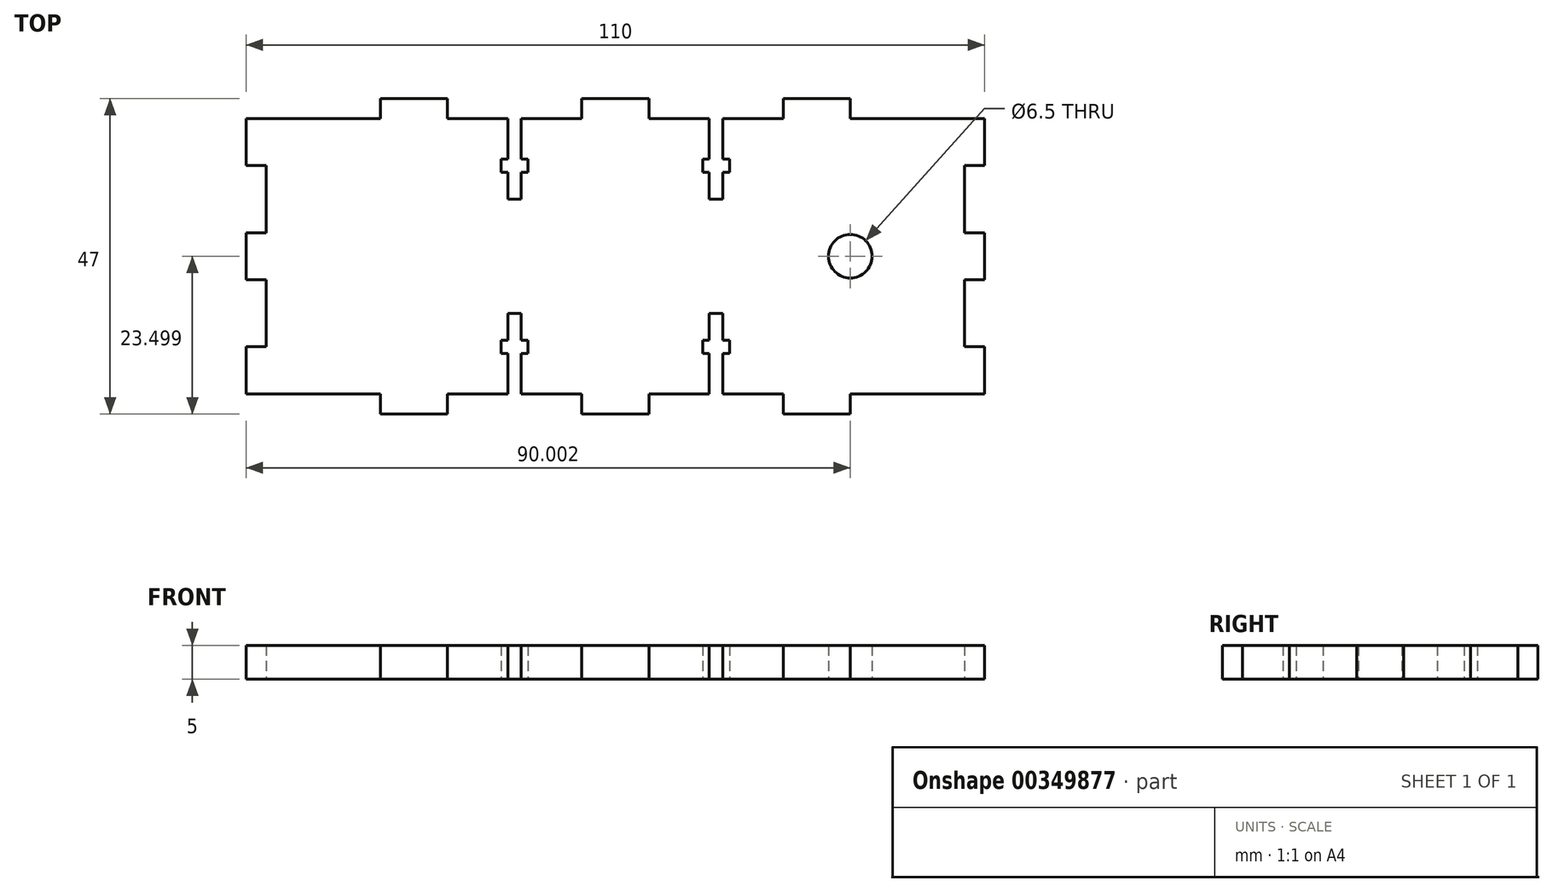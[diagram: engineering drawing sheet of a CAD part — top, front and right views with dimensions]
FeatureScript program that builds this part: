
annotation { "Feature Type Name" : "Feature", "Feature Type Description" : "" }
export const myFeature = defineFeature(function(context is Context, id is Id, definition is map)
    precondition{}
    {
        {
            var Q0;
            Q0=qCreatedBy(makeId("Top.planeOp"),FACE);
            var sketch = newSketch(context, id + "F0", { "sketchPlane" : qUnion([Q0])});
            skLineSegment(sketch, "E0", {"start": v(-63.5, 47.22) * mm, "end": v(-63.5, 40.22) * mm});
            skLineSegment(sketch, "E1", {"start": v(-63.5, 40.22) * mm, "end": v(-60.5, 40.22) * mm});
            skLineSegment(sketch, "E2", {"start": v(-60.5, 40.22) * mm, "end": v(-60.5, 30.22) * mm});
            skLineSegment(sketch, "E3", {"start": v(-60.5, 30.22) * mm, "end": v(-63.5, 30.22) * mm});
            skLineSegment(sketch, "E4", {"start": v(-63.5, 30.22) * mm, "end": v(-63.5, 23.22) * mm});
            skLineSegment(sketch, "E5", {"start": v(-63.5, 23.22) * mm, "end": v(-60.5, 23.22) * mm});
            skLineSegment(sketch, "E6", {"start": v(-60.5, 23.22) * mm, "end": v(-60.5, 13.22) * mm});
            skLineSegment(sketch, "E7", {"start": v(-60.5, 13.22) * mm, "end": v(-63.5, 13.22) * mm});
            skLineSegment(sketch, "E8", {"start": v(-63.5, 13.22) * mm, "end": v(-63.5, 6.22) * mm});
            skLineSegment(sketch, "E9", {"start": v(-63.5, 6.22) * mm, "end": v(-43.5, 6.22) * mm});
            skLineSegment(sketch, "E10", {"start": v(-43.5, 6.22) * mm, "end": v(-43.5, 3.22) * mm});
            skLineSegment(sketch, "E11", {"start": v(-43.5, 3.22) * mm, "end": v(-33.5, 3.22) * mm});
            skLineSegment(sketch, "E12", {"start": v(-33.5, 3.22) * mm, "end": v(-33.5, 6.22) * mm});
            skLineSegment(sketch, "E13", {"start": v(-33.5, 6.22) * mm, "end": v(-24.5, 6.22) * mm});
            skLineSegment(sketch, "E14", {"start": v(-24.5, 6.22) * mm, "end": v(-24.5, 12.22) * mm});
            skLineSegment(sketch, "E15", {"start": v(-24.5, 12.22) * mm, "end": v(-25.5, 12.22) * mm});
            skLineSegment(sketch, "E16", {"start": v(-25.5, 12.22) * mm, "end": v(-25.5, 14.22) * mm});
            skLineSegment(sketch, "E17", {"start": v(-25.5, 14.22) * mm, "end": v(-24.5, 14.22) * mm});
            skLineSegment(sketch, "E18", {"start": v(-24.5, 14.22) * mm, "end": v(-24.5, 18.22) * mm});
            skLineSegment(sketch, "E19", {"start": v(-24.5, 18.22) * mm, "end": v(-22.5, 18.22) * mm});
            skLineSegment(sketch, "E20", {"start": v(-22.5, 18.22) * mm, "end": v(-22.5, 14.22) * mm});
            skLineSegment(sketch, "E21", {"start": v(-22.5, 14.22) * mm, "end": v(-21.5, 14.22) * mm});
            skLineSegment(sketch, "E22", {"start": v(-21.5, 14.22) * mm, "end": v(-21.5, 12.22) * mm});
            skLineSegment(sketch, "E23", {"start": v(-21.5, 12.22) * mm, "end": v(-22.5, 12.22) * mm});
            skLineSegment(sketch, "E24", {"start": v(-22.5, 12.22) * mm, "end": v(-22.5, 6.22) * mm});
            skLineSegment(sketch, "E25", {"start": v(-22.5, 6.22) * mm, "end": v(-13.5, 6.22) * mm});
            skLineSegment(sketch, "E26", {"start": v(-13.5, 6.22) * mm, "end": v(-13.5, 3.22) * mm});
            skLineSegment(sketch, "E27", {"start": v(-13.5, 3.22) * mm, "end": v(-3.5, 3.22) * mm});
            skLineSegment(sketch, "E28", {"start": v(-3.5, 3.22) * mm, "end": v(-3.5, 6.22) * mm});
            skLineSegment(sketch, "E29", {"start": v(-3.5, 6.22) * mm, "end": v(5.5, 6.22) * mm});
            skLineSegment(sketch, "E30", {"start": v(5.5, 6.22) * mm, "end": v(5.5, 12.22) * mm});
            skLineSegment(sketch, "E31", {"start": v(5.5, 12.22) * mm, "end": v(4.5, 12.22) * mm});
            skLineSegment(sketch, "E32", {"start": v(4.5, 12.22) * mm, "end": v(4.5, 14.22) * mm});
            skLineSegment(sketch, "E33", {"start": v(4.5, 14.22) * mm, "end": v(5.5, 14.22) * mm});
            skLineSegment(sketch, "E34", {"start": v(5.5, 14.22) * mm, "end": v(5.5, 18.22) * mm});
            skLineSegment(sketch, "E35", {"start": v(5.5, 18.22) * mm, "end": v(7.5, 18.22) * mm});
            skLineSegment(sketch, "E36", {"start": v(7.5, 18.22) * mm, "end": v(7.5, 14.22) * mm});
            skLineSegment(sketch, "E37", {"start": v(7.5, 14.22) * mm, "end": v(8.5, 14.22) * mm});
            skLineSegment(sketch, "E38", {"start": v(8.5, 14.22) * mm, "end": v(8.5, 12.22) * mm});
            skLineSegment(sketch, "E39", {"start": v(8.5, 12.22) * mm, "end": v(7.5, 12.22) * mm});
            skLineSegment(sketch, "E40", {"start": v(7.5, 12.22) * mm, "end": v(7.5, 6.22) * mm});
            skLineSegment(sketch, "E41", {"start": v(7.5, 6.22) * mm, "end": v(16.5, 6.22) * mm});
            skLineSegment(sketch, "E42", {"start": v(16.5, 6.22) * mm, "end": v(16.5, 3.22) * mm});
            skLineSegment(sketch, "E43", {"start": v(16.5, 3.22) * mm, "end": v(26.5, 3.22) * mm});
            skLineSegment(sketch, "E44", {"start": v(26.5, 3.22) * mm, "end": v(26.5, 6.22) * mm});
            skLineSegment(sketch, "E45", {"start": v(26.5, 6.22) * mm, "end": v(46.5, 6.22) * mm});
            skLineSegment(sketch, "E46", {"start": v(46.5, 6.22) * mm, "end": v(46.5, 13.22) * mm});
            skLineSegment(sketch, "E47", {"start": v(46.5, 13.22) * mm, "end": v(43.5, 13.22) * mm});
            skLineSegment(sketch, "E48", {"start": v(43.5, 13.22) * mm, "end": v(43.5, 23.22) * mm});
            skLineSegment(sketch, "E49", {"start": v(46.5, 23.22) * mm, "end": v(43.5, 23.22) * mm});
            skLineSegment(sketch, "E50", {"start": v(46.5, 23.22) * mm, "end": v(46.5, 30.22) * mm});
            skLineSegment(sketch, "E51", {"start": v(46.5, 30.22) * mm, "end": v(43.5, 30.22) * mm});
            skLineSegment(sketch, "E52", {"start": v(43.5, 30.22) * mm, "end": v(43.5, 40.22) * mm});
            skLineSegment(sketch, "E53", {"start": v(43.5, 40.22) * mm, "end": v(46.5, 40.22) * mm});
            skLineSegment(sketch, "E54", {"start": v(46.5, 40.22) * mm, "end": v(46.5, 47.22) * mm});
            skLineSegment(sketch, "E55", {"start": v(46.5, 47.22) * mm, "end": v(26.5, 47.22) * mm});
            skLineSegment(sketch, "E56", {"start": v(26.5, 47.22) * mm, "end": v(26.5, 50.22) * mm});
            skLineSegment(sketch, "E57", {"start": v(26.5, 50.22) * mm, "end": v(16.5, 50.22) * mm});
            skLineSegment(sketch, "E58", {"start": v(16.5, 50.22) * mm, "end": v(16.5, 47.22) * mm});
            skLineSegment(sketch, "E59", {"start": v(7.5, 47.22) * mm, "end": v(16.5, 47.22) * mm});
            skLineSegment(sketch, "E60", {"start": v(7.5, 47.22) * mm, "end": v(7.5, 41.22) * mm});
            skLineSegment(sketch, "E61", {"start": v(7.5, 41.22) * mm, "end": v(8.5, 41.22) * mm});
            skLineSegment(sketch, "E62", {"start": v(8.5, 41.22) * mm, "end": v(8.5, 39.22) * mm});
            skLineSegment(sketch, "E63", {"start": v(8.5, 39.22) * mm, "end": v(7.5, 39.22) * mm});
            skLineSegment(sketch, "E64", {"start": v(7.5, 39.22) * mm, "end": v(7.5, 35.22) * mm});
            skLineSegment(sketch, "E65", {"start": v(7.5, 35.22) * mm, "end": v(5.5, 35.22) * mm});
            skLineSegment(sketch, "E66", {"start": v(5.5, 35.22) * mm, "end": v(5.5, 39.22) * mm});
            skLineSegment(sketch, "E67", {"start": v(5.5, 39.22) * mm, "end": v(4.5, 39.22) * mm});
            skLineSegment(sketch, "E68", {"start": v(4.5, 39.22) * mm, "end": v(4.5, 41.22) * mm});
            skLineSegment(sketch, "E69", {"start": v(4.5, 41.22) * mm, "end": v(5.5, 41.22) * mm});
            skLineSegment(sketch, "E70", {"start": v(5.5, 41.22) * mm, "end": v(5.5, 47.22) * mm});
            skLineSegment(sketch, "E71", {"start": v(5.5, 47.22) * mm, "end": v(-3.5, 47.22) * mm});
            skLineSegment(sketch, "E72", {"start": v(-3.5, 47.22) * mm, "end": v(-3.5, 50.22) * mm});
            skLineSegment(sketch, "E73", {"start": v(-3.5, 50.22) * mm, "end": v(-13.5, 50.22) * mm});
            skLineSegment(sketch, "E74", {"start": v(-13.5, 50.22) * mm, "end": v(-13.5, 47.22) * mm});
            skLineSegment(sketch, "E75", {"start": v(-13.5, 47.22) * mm, "end": v(-22.5, 47.22) * mm});
            skLineSegment(sketch, "E76", {"start": v(-22.5, 47.22) * mm, "end": v(-22.5, 41.22) * mm});
            skLineSegment(sketch, "E77", {"start": v(-22.5, 41.22) * mm, "end": v(-21.5, 41.22) * mm});
            skLineSegment(sketch, "E78", {"start": v(-21.5, 41.22) * mm, "end": v(-21.5, 39.22) * mm});
            skLineSegment(sketch, "E79", {"start": v(-21.5, 39.22) * mm, "end": v(-22.5, 39.22) * mm});
            skLineSegment(sketch, "E80", {"start": v(-22.5, 39.22) * mm, "end": v(-22.5, 35.22) * mm});
            skLineSegment(sketch, "E81", {"start": v(-22.5, 35.22) * mm, "end": v(-24.5, 35.22) * mm});
            skLineSegment(sketch, "E82", {"start": v(-24.5, 35.22) * mm, "end": v(-24.5, 39.22) * mm});
            skLineSegment(sketch, "E83", {"start": v(-24.5, 39.22) * mm, "end": v(-25.5, 39.22) * mm});
            skLineSegment(sketch, "E84", {"start": v(-25.5, 39.22) * mm, "end": v(-25.5, 41.22) * mm});
            skLineSegment(sketch, "E85", {"start": v(-25.5, 41.22) * mm, "end": v(-24.5, 41.22) * mm});
            skLineSegment(sketch, "E86", {"start": v(-24.5, 41.22) * mm, "end": v(-24.5, 47.22) * mm});
            skLineSegment(sketch, "E87", {"start": v(-24.5, 47.22) * mm, "end": v(-33.5, 47.22) * mm});
            skLineSegment(sketch, "E88", {"start": v(-33.5, 47.22) * mm, "end": v(-33.5, 50.22) * mm});
            skLineSegment(sketch, "E89", {"start": v(-33.5, 50.22) * mm, "end": v(-43.5, 50.22) * mm});
            skLineSegment(sketch, "E90", {"start": v(-43.5, 50.22) * mm, "end": v(-43.5, 47.22) * mm});
            skLineSegment(sketch, "E91", {"start": v(-43.5, 47.22) * mm, "end": v(-63.5, 47.22) * mm});
            skCircle(sketch, "E92", {"center": v(26.5, 26.72) * mm, "radius": 3.25 * mm});
            skPoint(sketch, "E92.centerSnap0", {"position": v(46.5, 26.72) * mm});
            skSolve(sketch);
        }
        {
            var Q0;
            Q0=makeQuery(id+"F0.imprint","IMPRINT",FACE,{"disambiguationData":[TD([[makeQuery(id+"F0.imprint","IMPRINT",EDGE,{"derivedFrom":sQuery(id+"F0.wireOp",EDGE,"E0")}),1.0]])]});
            extrude(context, id + "F1", {"entities" : qUnion([Q0]), "depth" : 5 * mm});
        }
    });
